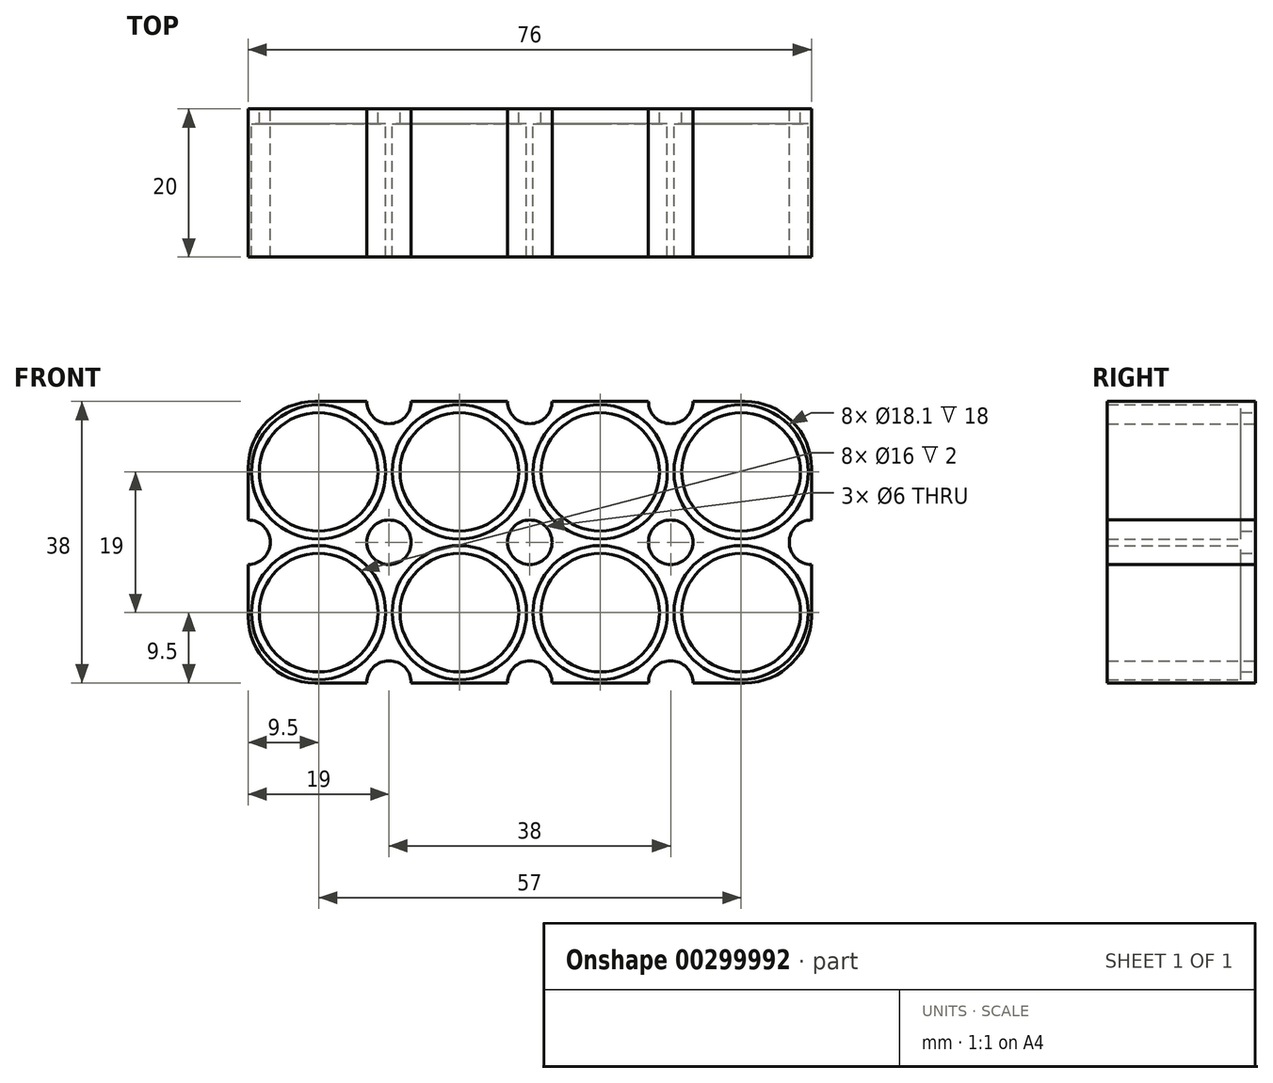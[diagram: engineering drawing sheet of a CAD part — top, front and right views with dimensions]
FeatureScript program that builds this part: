
annotation { "Feature Type Name" : "Feature", "Feature Type Description" : "" }
export const myFeature = defineFeature(function(context is Context, id is Id, definition is map)
    precondition{}
    {
        {
            var Q0;
            Q0=qCreatedBy(makeId("Front.planeOp"),FACE);
            var sketch = newSketch(context, id + "F0", { "sketchPlane" : qUnion([Q0])});
            skCircle(sketch, "E0", {"center": v(0, 0) * mm, "radius": 9.05 * mm});
            skCircle(sketch, "E1.0.1.0", {"center": v(0, 19) * mm, "radius": 9.05 * mm});
            skCircle(sketch, "E1.1.0.0", {"center": v(19, 0) * mm, "radius": 9.05 * mm});
            skCircle(sketch, "E1.1.1.0", {"center": v(19, 19) * mm, "radius": 9.05 * mm});
            skCircle(sketch, "E1.2.0.0", {"center": v(38, 0) * mm, "radius": 9.05 * mm});
            skCircle(sketch, "E1.2.1.0", {"center": v(38, 19) * mm, "radius": 9.05 * mm});
            skCircle(sketch, "E1.3.0.0", {"center": v(57, 0) * mm, "radius": 9.05 * mm});
            skCircle(sketch, "E1.3.1.0", {"center": v(57, 19) * mm, "radius": 9.05 * mm});
            skLineSegment(sketch, "E1.direction1", {"start": v(0, 0) * mm, "end": v(19, 0) * mm, "construction": true});
            skLineSegment(sketch, "E1.direction2", {"start": v(0, 0) * mm, "end": v(0, 19) * mm, "construction": true});
            skLineSegment(sketch, "E2.bottom", {"start": v(-0.5, 28.5) * mm, "end": v(6.5, 28.5) * mm});
            skLineSegment(sketch, "E2.top", {"start": v(-0.5, -9.5) * mm, "end": v(6.5, -9.5) * mm});
            skLineSegment(sketch, "E2.left", {"start": v(-9.5, 19.5) * mm, "end": v(-9.5, 12.5) * mm});
            skLineSegment(sketch, "E2.right", {"start": v(66.5, 19.5) * mm, "end": v(66.5, 12.5) * mm});
            skPoint(sketch, "E3.visualSharp", {"position": v(-9.5, 28.5) * mm});
            skArc(sketch, "E3.filletArc", {"start": v(-0.5, 28.5) * mm, "mid": v(-6.86, 25.86) * mm, "end": v(-9.5, 19.5) * mm});
            skPoint(sketch, "E4.visualSharp", {"position": v(66.5, 28.5) * mm});
            skArc(sketch, "E4.filletArc", {"start": v(66.5, 19.5) * mm, "mid": v(63.86, 25.86) * mm, "end": v(57.5, 28.5) * mm});
            skPoint(sketch, "E5.visualSharp", {"position": v(66.5, -9.5) * mm});
            skArc(sketch, "E5.filletArc", {"start": v(57.5, -9.5) * mm, "mid": v(63.86, -6.86) * mm, "end": v(66.5, -0.5) * mm});
            skPoint(sketch, "E6.visualSharp", {"position": v(-9.5, -9.5) * mm});
            skArc(sketch, "E6.filletArc", {"start": v(-9.5, -0.5) * mm, "mid": v(-6.86, -6.86) * mm, "end": v(-0.5, -9.5) * mm});
            skCircle(sketch, "E7", {"center": v(9.5, 9.5) * mm, "radius": 3 * mm});
            skCircle(sketch, "E8", {"center": v(28.5, 9.5) * mm, "radius": 3 * mm});
            skCircle(sketch, "E9", {"center": v(47.5, 9.5) * mm, "radius": 3 * mm});
            skArc(sketch, "E10", {"start": v(6.5, 28.5) * mm, "mid": v(9.5, 25.5) * mm, "end": v(12.5, 28.5) * mm});
            skArc(sketch, "E11", {"start": v(25.5, 28.5) * mm, "mid": v(28.5, 25.5) * mm, "end": v(31.5, 28.5) * mm});
            skArc(sketch, "E12", {"start": v(44.5, 28.5) * mm, "mid": v(47.5, 25.5) * mm, "end": v(50.5, 28.5) * mm});
            skArc(sketch, "E13", {"start": v(12.5, -9.5) * mm, "mid": v(9.5, -6.5) * mm, "end": v(6.5, -9.5) * mm});
            skArc(sketch, "E14", {"start": v(31.5, -9.5) * mm, "mid": v(28.5, -6.5) * mm, "end": v(25.5, -9.5) * mm});
            skArc(sketch, "E15", {"start": v(50.5, -9.5) * mm, "mid": v(47.5, -6.5) * mm, "end": v(44.5, -9.5) * mm});
            skArc(sketch, "E16", {"start": v(66.5, 12.5) * mm, "mid": v(63.5, 9.5) * mm, "end": v(66.5, 6.5) * mm});
            skArc(sketch, "E17", {"start": v(-9.5, 6.5) * mm, "mid": v(-6.5, 9.5) * mm, "end": v(-9.5, 12.5) * mm});
            skLineSegment(sketch, "E18.trimOffspring", {"start": v(12.5, 28.5) * mm, "end": v(25.5, 28.5) * mm});
            skLineSegment(sketch, "E19.trimOffspring", {"start": v(31.5, 28.5) * mm, "end": v(44.5, 28.5) * mm});
            skLineSegment(sketch, "E20.trimOffspring", {"start": v(50.5, 28.5) * mm, "end": v(57.5, 28.5) * mm});
            skLineSegment(sketch, "E21.trimOffspring", {"start": v(66.5, 6.5) * mm, "end": v(66.5, -0.5) * mm});
            skLineSegment(sketch, "E22.trimOffspring", {"start": v(50.5, -9.5) * mm, "end": v(57.5, -9.5) * mm});
            skLineSegment(sketch, "E23.trimOffspring", {"start": v(31.5, -9.5) * mm, "end": v(44.5, -9.5) * mm});
            skLineSegment(sketch, "E24.trimOffspring", {"start": v(12.5, -9.5) * mm, "end": v(25.5, -9.5) * mm});
            skLineSegment(sketch, "E25.trimOffspring", {"start": v(-9.5, 6.5) * mm, "end": v(-9.5, -0.5) * mm});
            skSolve(sketch);
        }
        {
            var Q0;
            Q0 = qSketchRegion(id + "F0", true);
            extrude(context, id + "F1", {"entities" : qUnion([Q0]), "depth" : 20 * mm});
        }
        {
            var Q0;
            Q0=makeQuery(id+"F0.imprint","IMPRINT",FACE,{"disambiguationData":[TD([[makeQuery(id+"F0.imprint","IMPRINT",EDGE,{"derivedFrom":sQuery(id+"F0.wireOp",EDGE,"E0")}),-1.0]])]});
            var sketch = newSketch(context, id + "F2", { "sketchPlane" : qUnion([Q0])});
            skCircle(sketch, "E26", {"center": v(57, 0) * mm, "radius": 9.05 * mm});
            skCircle(sketch, "E27.0.1.0", {"center": v(57, 19) * mm, "radius": 9.05 * mm});
            skCircle(sketch, "E27.1.0.0", {"center": v(38, 0) * mm, "radius": 9.05 * mm});
            skCircle(sketch, "E27.1.1.0", {"center": v(38, 19) * mm, "radius": 9.05 * mm});
            skCircle(sketch, "E27.2.0.0", {"center": v(19, 0) * mm, "radius": 9.05 * mm});
            skCircle(sketch, "E27.2.1.0", {"center": v(19, 19) * mm, "radius": 9.05 * mm});
            skCircle(sketch, "E27.3.0.0", {"center": v(0, 0) * mm, "radius": 9.05 * mm});
            skCircle(sketch, "E27.3.1.0", {"center": v(0, 19) * mm, "radius": 9.05 * mm});
            skLineSegment(sketch, "E27.direction1", {"start": v(57, 0) * mm, "end": v(38, 0) * mm, "construction": true});
            skLineSegment(sketch, "E27.direction2", {"start": v(57, 0) * mm, "end": v(57, 19) * mm, "construction": true});
            skCircle(sketch, "E28", {"center": v(57, 0) * mm, "radius": 8 * mm});
            skCircle(sketch, "E29.0.1.0", {"center": v(57, 19) * mm, "radius": 8 * mm});
            skCircle(sketch, "E29.1.0.0", {"center": v(38, 0) * mm, "radius": 8 * mm});
            skCircle(sketch, "E29.1.1.0", {"center": v(38, 19) * mm, "radius": 8 * mm});
            skCircle(sketch, "E29.2.0.0", {"center": v(19, 0) * mm, "radius": 8 * mm});
            skCircle(sketch, "E29.2.1.0", {"center": v(19, 19) * mm, "radius": 8 * mm});
            skCircle(sketch, "E29.3.0.0", {"center": v(0, 0) * mm, "radius": 8 * mm});
            skCircle(sketch, "E29.3.1.0", {"center": v(0, 19) * mm, "radius": 8 * mm});
            skSolve(sketch);
        }
        {
            var Q0;
            Q0 = qSketchRegion(id + "F2", true);
            extrude(context, id + "F3", {"entities" : qUnion([Q0]), "operationType" : NewBodyOperationType.ADD, "depth" : 2 * mm});
        }
    });
